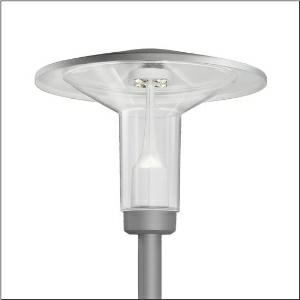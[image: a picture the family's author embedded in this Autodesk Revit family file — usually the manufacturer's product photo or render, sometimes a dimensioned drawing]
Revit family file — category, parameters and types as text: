
# Revit family: laterne_iq___p1_0a_5xa5255ff14hp_b565
name_source: partatom
category: Lighting Fixtures
units: mm (PartAtom-declared; Revit-internal decimal feet)

## family parameters
Cut with Voids When Loaded = No
Host = Face
Light Source = No
Part Type = Normal
Room Calculation Point = No
Round Connector Dimension = Use Diameter
Shared = No

## types (1)
- --- (1 x LED, 4700 lm, 33.6 W, 3000K)
    Apparent Load = 34 VA
    CIE Flux Codes = 34 64 92 97 100
    Color Rendering = 70
    Color Temperature = 3000K
    Default Elevation = 1800 mm
    Description = Lantern iQ, mast luminaire, Module 540 iQ-SR, primary light control with 3 zone facetted reflector, of plastic, silver coated, highly specular, structured, primary optical cover: cover, of PMMA, transparent, light distribution: P1.0a, light emission: direct distribution, primary light characteristic: strongly asymmetric, installation type: post-top, LED, High Power LED, rated luminous flux: 4.700lm, luminous efficacy: 140lm/W, light colour: 730, colour temperature: 3000K, control gear: iQ Street-Remote, control: pre-setting: logarithmic dimming characteristic, Street-Remote, Auto-Match, Temp-Guard, Lumen-Switch, Night-Set, Smart-Wire, Light-Fading, Desk-Remote (wireless, voltage-free reading and setting of iQ features in the workshop via application-optimized NFC function/RFID function), optimised constant luminous flux control (CLO 2.0), with terminal, 6-pole, max. 2.5mm², mains connection: 230..240V, AC, 50/60Hz, start of lifetime: 34W, end of service life: 36W, reduction: 15W, luminaire housing, upper part, of glass-fibre reinforced polyester, coated, Siteco® metallic grey (DB 702S), diameter: 750mm, height: 583mm, spigot size: d x l = 76 x 70mm (post-top) | with reducer (optional accessory) 60 x 70mm, mounting height: 3..5m, post-top mast mounting element, of diecast aluminium, coated, Siteco® metallic grey (DB 702S), Module 540 iQ-SR, traffic white (RAL 9016), equipment: Power, protection rating (complete): IP65, insulation class (complete): insulation class II (safety insulation), certification: CE, ENEC, VDE, packaging unit: 1 piece

Light Distribution: P1.0a
    Height = 583 mm
    Lamp = 1 x LED
    Lamp Light Flux = 4700 lm
    Lamp Power = 33.6 W
    Lamp count = 1
    Length = 750 mm
    Luminous efficacy = 140 lm/W
    Manufacturer = Siteco
    ModVariant = No
    Model = 5XA5255FF14HP
    Number of Poles = 1
    OnlyDefault = Yes
    Power Factor = 1
    Product Name = Laterne iQ | P1.0a
    Product group = mast luminaire | pylon top
    ProductGroupID = 6100
    Protection Class = Protection class II
    Protection Degree = IP 65
    RLX_Detail_Level = 1
    RLX_Emergency_Light_Flux = 0 lm
    RLX_Emergency_Type = 0
    RLX_Emergency_Type_DB = No
    RlxData = <blob elided: 34501 chars, md5=d8d9d4d1>
    Socket = socket
    Standby Power = 0 W
    System Light Flux = 4700 lm
    System Power = 34 W
    Type Comments = factory setting: luminous flux: 100 % | dim-lin: 254 | 695 mA
    Type Image = l_1006050.jpg
    URL = http://relux.com
    VarID = @adj_193392
    Voltage = 0 V
    Weight = 0.00 kg
    Width = 0 mm  [stored 0 ft]

note: [stored X ft] marks values corroborated as IEEE doubles in the binary element streams (Revit-internal decimal feet)

## geometry (parser evidence)
native form markers: Blend x4, Sweep x11
no freeform markers — native parametric forms only
